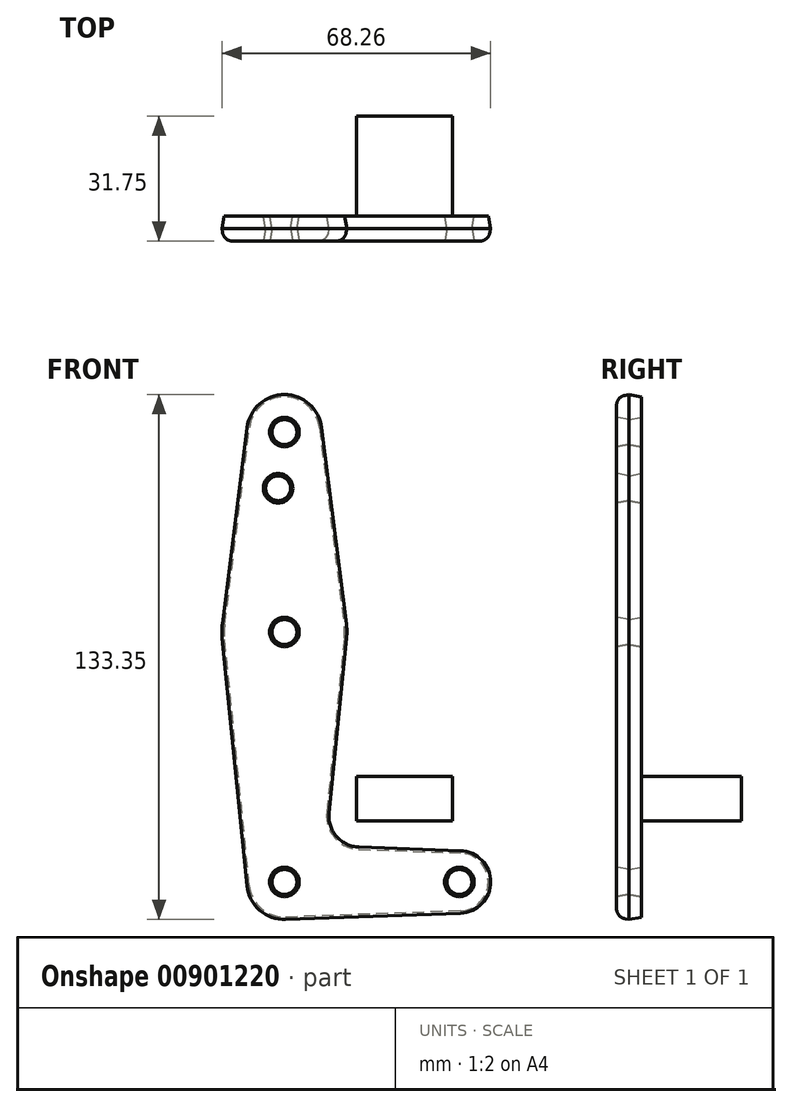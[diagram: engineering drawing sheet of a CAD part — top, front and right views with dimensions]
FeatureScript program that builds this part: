
annotation { "Feature Type Name" : "Feature", "Feature Type Description" : "" }
export const myFeature = defineFeature(function(context is Context, id is Id, definition is map)
    precondition{}
    {
        {
            var Q0;
            Q0=qCreatedBy(makeId("Front.planeOp"),FACE);
            var sketch = newSketch(context, id + "F0", { "sketchPlane" : qUnion([Q0])});
            skLineSegment(sketch, "E0", {"start": v(44.45, 0) * mm, "end": v(0, 0) * mm, "construction": true});
            skLineSegment(sketch, "E1", {"start": v(0, 0) * mm, "end": v(0, 63.5) * mm, "construction": true});
            skLineSegment(sketch, "E2", {"start": v(0, 63.5) * mm, "end": v(0, 114.3) * mm, "construction": true});
            skCircle(sketch, "E3", {"center": v(0, 114.3) * mm, "radius": 9.53 * mm});
            skCircle(sketch, "E4", {"center": v(0, 63.5) * mm, "radius": 15.88 * mm});
            skCircle(sketch, "E5", {"center": v(0, 0) * mm, "radius": 9.53 * mm});
            skCircle(sketch, "E6", {"center": v(44.45, 0) * mm, "radius": 7.94 * mm});
            skLineSegment(sketch, "E7", {"start": v(18.97, 8.85) * mm, "end": v(44.73, 7.93) * mm});
            skLineSegment(sketch, "E8", {"start": v(0.34, -9.52) * mm, "end": v(44.73, -7.93) * mm});
            skLineSegment(sketch, "E9", {"start": v(9.45, 115.5) * mm, "end": v(15.75, 65.48) * mm});
            skLineSegment(sketch, "E10", {"start": v(-9.45, 115.5) * mm, "end": v(-15.75, 65.48) * mm});
            skLineSegment(sketch, "E11", {"start": v(15.8, 61.91) * mm, "end": v(11.34, 17.6) * mm});
            skLineSegment(sketch, "E12", {"start": v(-15.8, 61.91) * mm, "end": v(-9.48, -0.95) * mm});
            skPoint(sketch, "E13.newPointB", {"position": v(9.48, -0.95) * mm});
            skArc(sketch, "E13.filletArc", {"start": v(11.34, 17.6) * mm, "mid": v(13.26, 11.57) * mm, "end": v(18.97, 8.85) * mm});
            skCircle(sketch, "E14", {"center": v(0, 114.3) * mm, "radius": 3.18 * mm});
            skCircle(sketch, "E15", {"center": v(0, 63.5) * mm, "radius": 3.18 * mm});
            skCircle(sketch, "E16", {"center": v(0, 0) * mm, "radius": 3.18 * mm});
            skCircle(sketch, "E17", {"center": v(44.45, 0) * mm, "radius": 3.18 * mm});
            skCircle(sketch, "E18", {"center": v(-1.59, 100.03) * mm, "radius": 3.18 * mm});
            skSolve(sketch);
        }
        {
            var Q0;
            Q0=makeQuery(id+"F0.imprint","IMPRINT",FACE,{"disambiguationData":[TD([[makeQuery(id+"F0.imprint","IMPRINT",EDGE,{"derivedFrom":sQuery(id+"F0.wireOp",EDGE,"E14")}),-1.0]])]});
            var Q1;
            Q1=makeQuery(id+"F0.imprint","IMPRINT",FACE,{"disambiguationData":[TD([[makeQuery(id+"F0.imprint","IMPRINT",EDGE,{"derivedFrom":sQuery(id+"F0.wireOp",EDGE,"E16")}),-1.0]])]});
            var Q2;
            Q2=makeQuery(id+"F0.imprint","IMPRINT",FACE,{"disambiguationData":[TD([[makeQuery(id+"F0.imprint","IMPRINT",EDGE,{"derivedFrom":sQuery(id+"F0.wireOp",EDGE,"E17")}),-1.0]])]});
            var Q3;
            Q3=makeQuery(id+"F0.imprint","IMPRINT",FACE,{"disambiguationData":[TD([[makeQuery(id+"F0.imprint","IMPRINT",EDGE,{"derivedFrom":sQuery(id+"F0.wireOp",EDGE,"E15")}),-1.0]])]});
            var Q4;
            {var subQ0=sQuery(id+"F0.wireOp",EDGE,"E7");Q4=makeQuery(id+"F0.imprint","IMPRINT",FACE,{"disambiguationData":[TD([[makeQuery(id+"F0.imprint","IMPRINT",EDGE,{"derivedFrom":subQ0}),-1.0]])]});}
            var Q5;
            {var subQ1=sQuery(id+"F0.wireOp",EDGE,"E9");Q5=makeQuery(id+"F0.imprint","IMPRINT",FACE,{"disambiguationData":[TD([[makeQuery(id+"F0.imprint","IMPRINT",EDGE,{"derivedFrom":subQ1}),-1.0]])]});}
            extrude(context, id + "F1", {"entities" : qUnion([Q0, Q1, Q2, Q3, Q4, Q5]), "depth" : 6.35 * mm, "offsetDistance" : 25.4 * mm, "hasDraft" : true, "draftAngle" : 10 * degree, "draftPullDirection" : true, "symmetric" : true});
        }
        {
            var Q0;
            Q0=makeQuery(id+"F1.opExtrude","CAP_FACE",FACE,{"disambiguationData":[OSD([sQuery(id+"F0.wireOp",EDGE,"E3"),sQuery(id+"F0.wireOp",EDGE,"E4"),sQuery(id+"F0.wireOp",EDGE,"E5"),sQuery(id+"F0.wireOp",EDGE,"E6"),sQuery(id+"F0.wireOp",EDGE,"E7"),sQuery(id+"F0.wireOp",EDGE,"E8"),sQuery(id+"F0.wireOp",EDGE,"E9"),sQuery(id+"F0.wireOp",EDGE,"E10"),sQuery(id+"F0.wireOp",EDGE,"E11"),sQuery(id+"F0.wireOp",EDGE,"E12"),sQuery(id+"F0.wireOp",EDGE,"E13.filletArc"),sQuery(id+"F0.wireOp",EDGE,"E14"),sQuery(id+"F0.wireOp",EDGE,"E15"),sQuery(id+"F0.wireOp",EDGE,"E16"),sQuery(id+"F0.wireOp",EDGE,"E17"),sQuery(id+"F0.wireOp",EDGE,"E18")])],"isStart":true});
            var sketch = newSketch(context, id + "F2", { "sketchPlane" : qUnion([Q0])});
            skLineSegment(sketch, "E19.bottom", {"start": v(-42.7, 15.53) * mm, "end": v(-18.28, 15.53) * mm});
            skLineSegment(sketch, "E19.top", {"start": v(-42.7, 26.84) * mm, "end": v(-18.28, 26.84) * mm});
            skLineSegment(sketch, "E19.left", {"start": v(-42.7, 15.53) * mm, "end": v(-42.7, 26.84) * mm});
            skLineSegment(sketch, "E19.right", {"start": v(-18.28, 15.53) * mm, "end": v(-18.28, 26.84) * mm});
            skPoint(sketch, "E19.middle", {"position": v(-30.48, 21.18) * mm});
            skSolve(sketch);
        }
        {
            var Q0;
            Q0 = qSketchRegion(id + "F2", true);
            extrude(context, id + "F3", {"entities" : qUnion([Q0]), "depth" : 25.4 * mm, "offsetDistance" : 25.4 * mm});
        }
        {
            var Q0;
            Q0=makeQuery(id+"F1.opExtrude","CAP_EDGE",EDGE,{"disambiguationData":[OSD([sQuery(id+"F0.wireOp",EDGE,"E11")])],"isStart":false});
            var Q1;
            {var subQ0=makeQuery(id+"F1.opExtrude","SWEPT_FACE",FACE,{"disambiguationData":[OSD([sQuery(id+"F0.wireOp",EDGE,"E13.filletArc")])]});var subQ1=makeQuery(id+"F1.opExtrude","SWEPT_FACE",FACE,{"disambiguationData":[OSD([sQuery(id+"F0.wireOp",EDGE,"E11")])]});Q1=makeQuery(id+"F1.*.booleanUnion.opBoolean","MERGE",VERTEX,{"derivedFrom":[makeQuery(id+"F1.*.split.splitOp","SPLIT_SURFACE_INTERSECT",VERTEX,{"derivedFrom":[subQ1,subQ0]}),makeQuery(id+"F1.*.split.splitOp","SPLIT_SURFACE_INTERSECT",VERTEX,{"derivedFrom":[subQ1,subQ0],"isFromBackBody":true})]});}
            fillet(context, id + "F4", {"entities" : qUnion([Q0]), "tangentPropagation" : true, "radius" : 2.54 * mm, "defaultsChanged" : false, "vertexSettings" : [{ "vertex" : qUnion([Q1]), "vertexRadius" : { 'value' : try(12.7 * mm), 'expression' : ".5 in" }.value, "variableRho" : 0.5, "variableMagnitude" : 0.5 }], "allowEdgeOverflow" : false});
        }
    });
